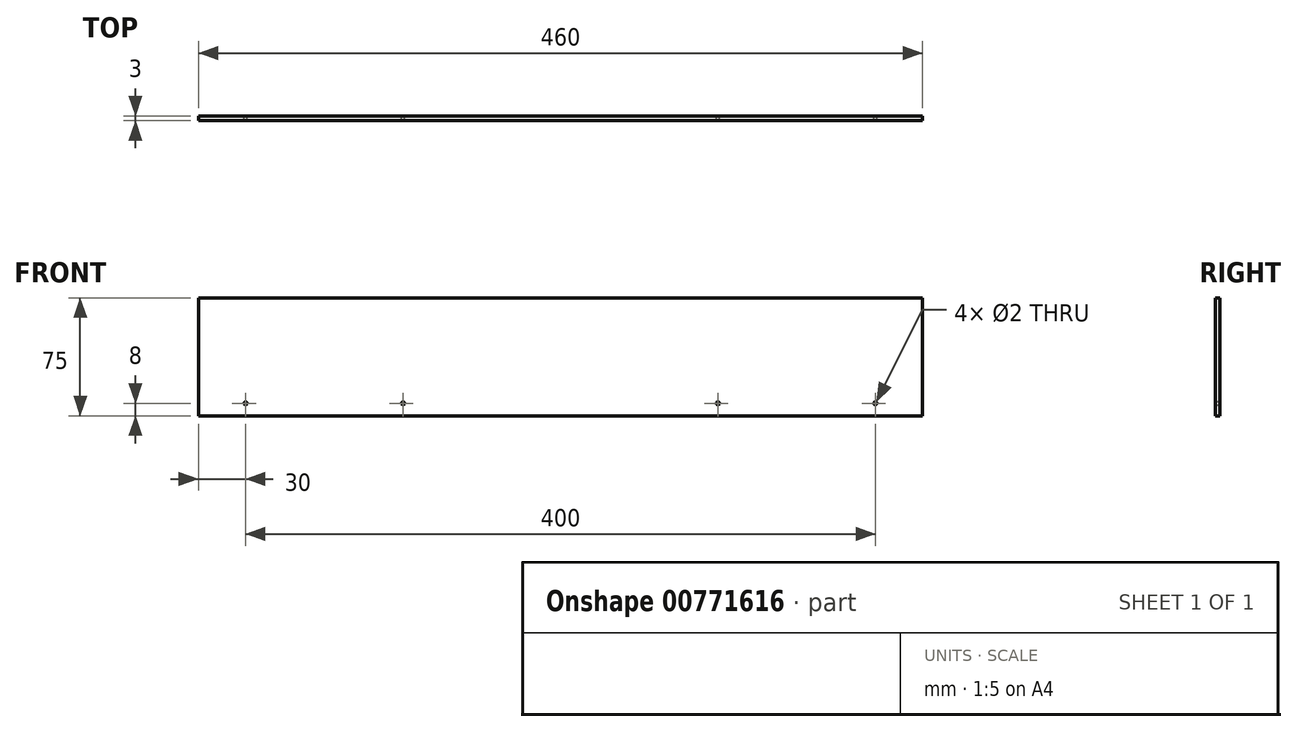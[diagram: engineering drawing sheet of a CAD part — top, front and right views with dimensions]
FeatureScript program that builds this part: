
annotation { "Feature Type Name" : "Feature", "Feature Type Description" : "" }
export const myFeature = defineFeature(function(context is Context, id is Id, definition is map)
    precondition{}
    {
        {
            var Q0;
            Q0=qCreatedBy(makeId("Front.planeOp"),FACE);
            var sketch = newSketch(context, id + "F0", { "sketchPlane" : qUnion([Q0])});
            skLineSegment(sketch, "E0.bottom", {"start": v(230, 37.5) * mm, "end": v(-230, 37.5) * mm});
            skLineSegment(sketch, "E0.top", {"start": v(230, -37.5) * mm, "end": v(-230, -37.5) * mm});
            skLineSegment(sketch, "E0.left", {"start": v(230, 37.5) * mm, "end": v(230, -37.5) * mm});
            skLineSegment(sketch, "E0.right", {"start": v(-230, 37.5) * mm, "end": v(-230, -37.5) * mm});
            skPoint(sketch, "E0.middle", {"position": v(0, 0) * mm});
            skCircle(sketch, "E1", {"center": v(-200, -29.5) * mm, "radius": 1 * mm});
            skCircle(sketch, "E2", {"center": v(200, -29.5) * mm, "radius": 1 * mm});
            skCircle(sketch, "E3", {"center": v(-100, -29.5) * mm, "radius": 1 * mm});
            skCircle(sketch, "E4", {"center": v(100, -29.5) * mm, "radius": 1 * mm});
            skSolve(sketch);
        }
        {
            var Q0;
            Q0=makeQuery(id+"F0.imprint","IMPRINT",FACE,{"disambiguationData":[TD([[makeQuery(id+"F0.imprint","IMPRINT",EDGE,{"derivedFrom":sQuery(id+"F0.wireOp",EDGE,"E0.bottom")}),1.0]])]});
            extrude(context, id + "F1", {"entities" : qUnion([Q0]), "depth" : 3 * mm, "offsetDistance" : 25 * mm});
        }
    });
